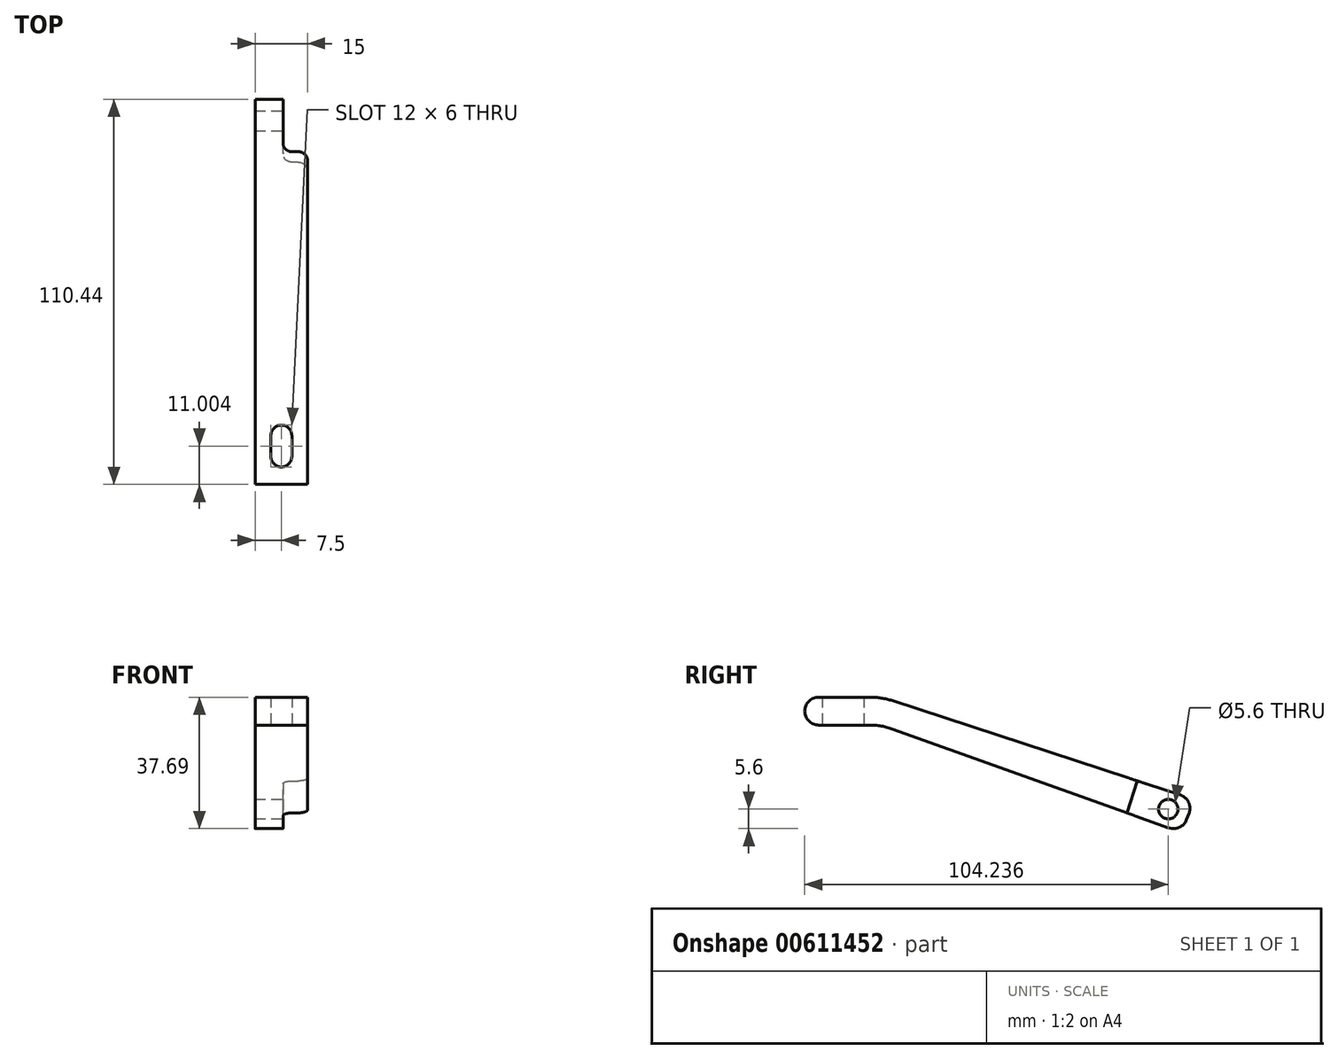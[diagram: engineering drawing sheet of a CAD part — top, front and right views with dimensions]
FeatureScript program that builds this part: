
annotation { "Feature Type Name" : "Feature", "Feature Type Description" : "" }
export const myFeature = defineFeature(function(context is Context, id is Id, definition is map)
    precondition{}
    {
        {
            var Q0;
            Q0=qCreatedBy(makeId("Right.planeOp"),FACE);
            var sketch = newSketch(context, id + "F0", { "sketchPlane" : qUnion([Q0])});
            skLineSegment(sketch, "E0", {"start": v(-66.99, 8) * mm, "end": v(-44.99, 8) * mm});
            skLineSegment(sketch, "E1", {"start": v(-44.99, 8) * mm, "end": v(44.68, -21.34) * mm});
            skLineSegment(sketch, "E2", {"start": v(43.38, -24.77) * mm, "end": v(42.3, -27.6) * mm});
            skLineSegment(sketch, "E3", {"start": v(41.09, -30.77) * mm, "end": v(-44.99, 0) * mm});
            skLineSegment(sketch, "E4", {"start": v(-44.99, 0) * mm, "end": v(-66.99, 0) * mm});
            skLineSegment(sketch, "E5", {"start": v(-66.99, 8) * mm, "end": v(-66.99, 0) * mm});
            skPoint(sketch, "E6.visualSharp", {"position": v(45.27, -19.8) * mm});
            skPoint(sketch, "E7.visualSharp", {"position": v(41.13, -30.67) * mm});
            skLineSegment(sketch, "E8", {"start": v(42.47, -27.15) * mm, "end": v(39.03, -36.17) * mm, "construction": true});
            skPoint(sketch, "E9.orphan", {"position": v(44.36, -31.94) * mm});
            skPoint(sketch, "E10.orphan", {"position": v(37.44, -29.47) * mm});
            skPoint(sketch, "E11.orphan", {"position": v(41.21, -20.2) * mm});
            skLineSegment(sketch, "E12", {"start": v(44.68, -21.34) * mm, "end": v(41.09, -30.77) * mm});
            skSolve(sketch);
        }
        {
            var Q0;
            Q0=makeQuery(id+"F0.imprint","IMPRINT",FACE,{"disambiguationData":[TD([[makeQuery(id+"F0.imprint","IMPRINT",EDGE,{"derivedFrom":sQuery(id+"F0.wireOp",EDGE,"E0")}),-1.0]])]});
            extrude(context, id + "F1", {"entities" : qUnion([Q0]), "depth" : 15 * mm, "offsetDistance" : 25 * mm});
        }
        {
            var Q0;
            Q0=makeQuery(id+"F1.opExtrude","SWEPT_FACE",FACE,{"disambiguationData":[OSD([sQuery(id+"F0.wireOp",EDGE,"E4")])]});
            var sketch = newSketch(context, id + "F2", { "sketchPlane" : qUnion([Q0])});
            skPoint(sketch, "E13.positionSnap0", {"position": v(15, 58.25) * mm});
            skArc(sketch, "E14", {"start": v(4.5, 52.99) * mm, "mid": v(7.5, 49.99) * mm, "end": v(10.5, 52.99) * mm});
            skArc(sketch, "E15", {"start": v(10.5, 58.99) * mm, "mid": v(7.5, 61.99) * mm, "end": v(4.5, 58.99) * mm});
            skLineSegment(sketch, "E16", {"start": v(10.5, 58.99) * mm, "end": v(10.5, 52.99) * mm});
            skLineSegment(sketch, "E17", {"start": v(4.5, 52.99) * mm, "end": v(4.5, 58.99) * mm});
            skLineSegment(sketch, "E18", {"start": v(7.5, 52.99) * mm, "end": v(7.5, 58.99) * mm, "construction": true});
            skPoint(sketch, "E19", {"position": v(7.5, 55.99) * mm});
            skLineSegment(sketch, "E20", {"start": v(7.5, 44.99) * mm, "end": v(7.5, 66.99) * mm, "construction": true});
            skSolve(sketch);
        }
        {
            var Q0;
            Q0=makeQuery(id+"F2.imprint","IMPRINT",FACE,{"disambiguationData":[TD([[makeQuery(id+"F2.imprint","IMPRINT",EDGE,{"derivedFrom":sQuery(id+"F2.wireOp",EDGE,"E14")}),1.0]])]});
            extrude(context, id + "F3", {"entities" : qUnion([Q0]), "operationType" : NewBodyOperationType.REMOVE, "oppositeDirection" : true, "depth" : 25 * mm, "offsetDistance" : 25 * mm});
        }
        {
            var Q0;
            Q0=makeQuery(id+"F1.opExtrude","SWEPT_EDGE",EDGE,{"disambiguationData":[OSD([sQuery(id+"F0.wireOp",EDGE,"E4"),sQuery(id+"F0.wireOp",EDGE,"E5")])]});
            var Q1;
            Q1=makeQuery(id+"F1.opExtrude","SWEPT_EDGE",EDGE,{"disambiguationData":[OSD([sQuery(id+"F0.wireOp",EDGE,"E0"),sQuery(id+"F0.wireOp",EDGE,"E5")])]});
            fillet(context, id + "F4", {"entities" : qUnion([Q0, Q1]), "radius" : 4 * mm, "tangentPropagation" : true, "allowEdgeOverflow" : false});
        }
        {
            var Q0;
            Q0=makeQuery(id+"F1.opExtrude","SWEPT_FACE",FACE,{"disambiguationData":[OSD([sQuery(id+"F0.wireOp",EDGE,"E1")])]});
            var sketch = newSketch(context, id + "F5", { "sketchPlane" : qUnion([Q0])});
            skPoint(sketch, "E21.startSnap0", {"position": v(14.98, 48.96) * mm});
            skLineSegment(sketch, "E22.bottom", {"start": v(7.98, 31.96) * mm, "end": v(21.98, 31.96) * mm});
            skLineSegment(sketch, "E22.top", {"start": v(7.98, 65.96) * mm, "end": v(21.98, 65.96) * mm});
            skLineSegment(sketch, "E22.left", {"start": v(7.98, 31.96) * mm, "end": v(7.98, 65.96) * mm});
            skLineSegment(sketch, "E22.right", {"start": v(21.98, 31.96) * mm, "end": v(21.98, 65.96) * mm});
            skSolve(sketch);
        }
        {
            var Q0;
            {var subQ0=sQuery(id+"F5.wireOp",EDGE,"E22.bottom");Q0=makeQuery(id+"F5.imprint","IMPRINT",FACE,{"disambiguationData":[TD([[makeQuery(id+"F5.imprint","IMPRINT",EDGE,{"derivedFrom":subQ0}),1.0]])]});}
            var Q1;
            {var subQ0=sQuery(id+"F5.wireOp",EDGE,"E22.top");Q1=makeQuery(id+"F5.imprint","IMPRINT",FACE,{"disambiguationData":[TD([[makeQuery(id+"F5.imprint","IMPRINT",EDGE,{"derivedFrom":subQ0}),-1.0]])]});}
            extrude(context, id + "F6", {"entities" : qUnion([Q0, Q1]), "operationType" : NewBodyOperationType.REMOVE, "oppositeDirection" : true, "depth" : 25 * mm, "offsetDistance" : 25 * mm});
        }
        {
            var Q0;
            Q0=makeQuery(id+"F6.boolean.opBoolean","COPY",EDGE,{"derivedFrom":makeQuery(id+"F6.opExtrude","SWEPT_EDGE",EDGE,{"disambiguationData":[OSD([sQuery(id+"F5.wireOp",EDGE,"E22.bottom"),sQuery(id+"F5.wireOp",EDGE,"E22.left")])]})});
            var Q1;
            Q1=makeQuery(id+"F6.boolean.opBoolean","COPY",EDGE,{"derivedFrom":makeQuery(id+"F6.opExtrude","SWEPT_EDGE",EDGE,{"disambiguationData":[OSD([sQuery(id+"F5.wireOp",EDGE,"E22.bottom"),sQuery(id+"F5.wireOp",EDGE,"E22.right")])]})});
            var Q2;
            Q2=makeQuery(id+"F6.boolean.opBoolean","INTERSECT",EDGE,{"derivedFrom":[makeQuery(id+"F1.opExtrude","CAP_FACE",FACE,{"disambiguationData":[OSD([sQuery(id+"F0.wireOp",EDGE,"E0"),sQuery(id+"F0.wireOp",EDGE,"E1"),sQuery(id+"F0.wireOp",EDGE,"E3"),sQuery(id+"F0.wireOp",EDGE,"E4"),sQuery(id+"F0.wireOp",EDGE,"E5"),sQuery(id+"F0.wireOp",EDGE,"E12")])],"isStart":false}),makeQuery(id+"F6.opExtrude","SWEPT_FACE",FACE,{"disambiguationData":[OSD([sQuery(id+"F5.wireOp",EDGE,"E22.bottom")])]})]});
            fillet(context, id + "F7", {"entities" : qUnion([Q0, Q1, Q2]), "radius" : 2.6 * mm, "tangentPropagation" : true, "allowEdgeOverflow" : false});
        }
        {
            var Q0;
            Q0=makeQuery(id+"F1.opExtrude","CAP_FACE",FACE,{"disambiguationData":[OSD([sQuery(id+"F0.wireOp",EDGE,"E0"),sQuery(id+"F0.wireOp",EDGE,"E1"),sQuery(id+"F0.wireOp",EDGE,"E2"),sQuery(id+"F0.wireOp",EDGE,"E3"),sQuery(id+"F0.wireOp",EDGE,"E4"),sQuery(id+"F0.wireOp",EDGE,"E5"),sQuery(id+"F0.wireOp",EDGE,"E6.filletArc"),sQuery(id+"F0.wireOp",EDGE,"E7.filletArc")])],"isStart":false});
            var sketch = newSketch(context, id + "F8", { "sketchPlane" : qUnion([Q0])});
            skCircle(sketch, "E23", {"center": v(37.25, -24.09) * mm, "radius": 2.8 * mm});
            skSolve(sketch);
        }
        {
            var Q0;
            Q0=makeQuery(id+"F8.imprint","IMPRINT",FACE,{"disambiguationData":[TD([[makeQuery(id+"F8.imprint","IMPRINT",EDGE,{"derivedFrom":sQuery(id+"F8.wireOp",EDGE,"E23")}),1.0]])]});
            extrude(context, id + "F9", {"entities" : qUnion([Q0]), "operationType" : NewBodyOperationType.REMOVE, "oppositeDirection" : true, "depth" : 25 * mm, "offsetDistance" : 25 * mm});
        }
        {
            var Q0;
            Q0=makeQuery(id+"F1.opExtrude","SWEPT_EDGE",EDGE,{"disambiguationData":[OSD([sQuery(id+"F0.wireOp",EDGE,"E0"),sQuery(id+"F0.wireOp",EDGE,"E1")])]});
            var Q1;
            Q1=makeQuery(id+"F1.opExtrude","SWEPT_EDGE",EDGE,{"disambiguationData":[OSD([sQuery(id+"F0.wireOp",EDGE,"E3"),sQuery(id+"F0.wireOp",EDGE,"E4")])]});
            fillet(context, id + "F10", {"entities" : qUnion([Q0, Q1]), "radius" : 20 * mm, "tangentPropagation" : true, "allowEdgeOverflow" : false});
        }
        {
            var Q0;
            {var subQ0=sQuery(id+"F0.wireOp",EDGE,"E12");var subQ1=sQuery(id+"F0.wireOp",EDGE,"E3");Q0=makeQuery(id+"F6.boolean.opBoolean","SPLIT",EDGE,{"disambiguationData":[TD([makeQuery(id+"F6.opExtrude","SWEPT_FACE",FACE,{"disambiguationData":[OSD([sQuery(id+"F5.wireOp",EDGE,"E22.right")])]})])],"derivedFrom":makeQuery(id+"F1.opExtrude","SWEPT_EDGE",EDGE,{"disambiguationData":[OSD([subQ1,subQ0])]})});}
            var Q1;
            {var subQ0=sQuery(id+"F0.wireOp",EDGE,"E12");var subQ1=sQuery(id+"F0.wireOp",EDGE,"E3");Q1=makeQuery(id+"F6.boolean.opBoolean","SPLIT",EDGE,{"disambiguationData":[TD([makeQuery(id+"F6.opExtrude","SWEPT_FACE",FACE,{"disambiguationData":[OSD([sQuery(id+"F5.wireOp",EDGE,"E22.left")])]})])],"derivedFrom":makeQuery(id+"F1.opExtrude","SWEPT_EDGE",EDGE,{"disambiguationData":[OSD([subQ1,subQ0])]})});}
            var Q2;
            {var subQ0=sQuery(id+"F0.wireOp",EDGE,"E12");var subQ1=sQuery(id+"F0.wireOp",EDGE,"E1");Q2=makeQuery(id+"F6.boolean.opBoolean","SPLIT",EDGE,{"disambiguationData":[TD([makeQuery(id+"F6.opExtrude","SWEPT_FACE",FACE,{"disambiguationData":[OSD([sQuery(id+"F5.wireOp",EDGE,"E22.left")])]})])],"derivedFrom":makeQuery(id+"F1.opExtrude","SWEPT_EDGE",EDGE,{"disambiguationData":[OSD([subQ1,subQ0])]})});}
            var Q3;
            {var subQ0=sQuery(id+"F0.wireOp",EDGE,"E12");var subQ1=sQuery(id+"F0.wireOp",EDGE,"E1");Q3=makeQuery(id+"F6.boolean.opBoolean","SPLIT",EDGE,{"disambiguationData":[TD([makeQuery(id+"F6.opExtrude","SWEPT_FACE",FACE,{"disambiguationData":[OSD([sQuery(id+"F5.wireOp",EDGE,"E22.right")])]})])],"derivedFrom":makeQuery(id+"F1.opExtrude","SWEPT_EDGE",EDGE,{"disambiguationData":[OSD([subQ1,subQ0])]})});}
            fillet(context, id + "F11", {"entities" : qUnion([Q0, Q1, Q2, Q3]), "radius" : 4 * mm, "tangentPropagation" : true, "allowEdgeOverflow" : false});
        }
    });
